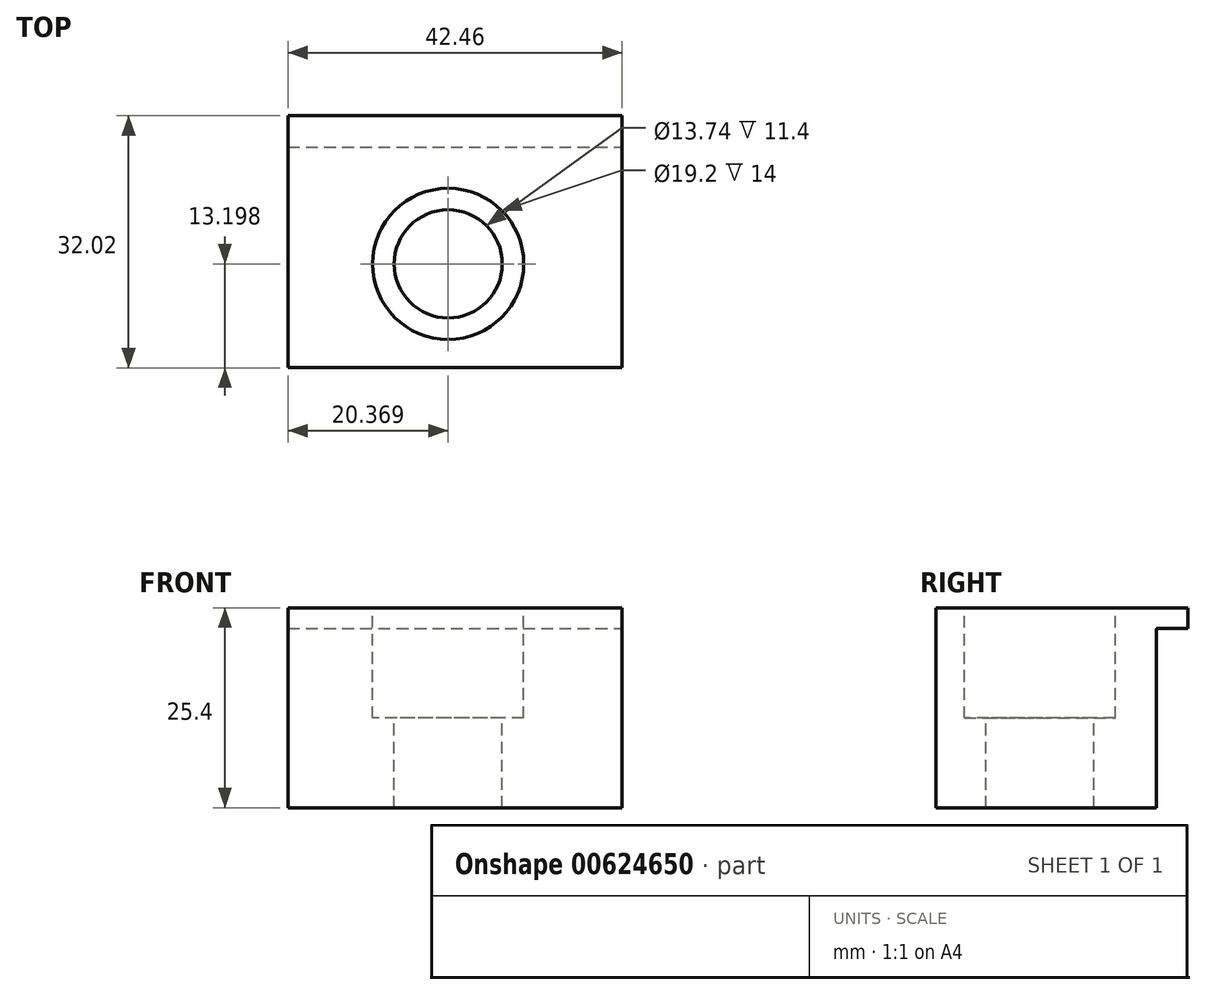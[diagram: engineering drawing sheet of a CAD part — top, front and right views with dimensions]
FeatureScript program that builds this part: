
annotation { "Feature Type Name" : "Feature", "Feature Type Description" : "" }
export const myFeature = defineFeature(function(context is Context, id is Id, definition is map)
    precondition{}
    {
        {
            var Q0;
            Q0=qCreatedBy(makeId("Top.planeOp"),FACE);
            var sketch = newSketch(context, id + "F0", { "sketchPlane" : qUnion([Q0])});
            skLineSegment(sketch, "E0.bottom", {"start": v(-47.59, 38.49) * mm, "end": v(-5.13, 38.49) * mm});
            skLineSegment(sketch, "E0.top", {"start": v(-47.59, 10.47) * mm, "end": v(-5.13, 10.47) * mm});
            skLineSegment(sketch, "E0.left", {"start": v(-47.59, 38.49) * mm, "end": v(-47.59, 10.47) * mm});
            skLineSegment(sketch, "E0.right", {"start": v(-5.13, 38.49) * mm, "end": v(-5.13, 10.47) * mm});
            skSolve(sketch);
        }
        {
            var Q0;
            Q0=makeQuery(id+"F0.imprint","IMPRINT",FACE,{"disambiguationData":[TD([[makeQuery(id+"F0.imprint","IMPRINT",EDGE,{"derivedFrom":sQuery(id+"F0.wireOp",EDGE,"E0.bottom")}),-1.0]])]});
            extrude(context, id + "F1", {"entities" : qUnion([Q0]), "depth" : 25.4 * mm, "offsetDistance" : 25 * mm});
        }
        {
            var Q0;
            Q0=makeQuery(id+"F1.opExtrude","CAP_FACE",FACE,{"disambiguationData":[OSD([sQuery(id+"F0.wireOp",EDGE,"E0.bottom"),sQuery(id+"F0.wireOp",EDGE,"E0.top"),sQuery(id+"F0.wireOp",EDGE,"E0.left"),sQuery(id+"F0.wireOp",EDGE,"E0.right")])],"isStart":false});
            var sketch = newSketch(context, id + "F2", { "sketchPlane" : qUnion([Q0])});
            skPoint(sketch, "E1", {"position": v(-27.22, 23.67) * mm});
            skSolve(sketch);
        }
        {
            var Q0;
            Q0=sQuery(id+"F2.wireOp",VERTEX,"E1");
            var Q1;
            Q1=makeQuery(id+"F1.opExtrude","SWEPT_BODY",BODY,{"disambiguationData":[OSD([sQuery(id+"F0.wireOp",EDGE,"E0.bottom"),sQuery(id+"F0.wireOp",EDGE,"E0.top"),sQuery(id+"F0.wireOp",EDGE,"E0.left"),sQuery(id+"F0.wireOp",EDGE,"E0.right")])]});
            hole(context, id + "F3", {"style" : HoleStyle.C_BORE, "endStyle" : HoleEndStyle.THROUGH, "holeDiameter" : 13.74 * mm, "cBoreDiameter" : 19.2 * mm, "cBoreDepth" : 14 * mm, "majorDiameter" : 5 * mm, "isTappedThrough" : true, "tappedDepth" : 12 * mm, "tapClearance" : 3, "startFromSketch" : true, "locations" : qUnion([Q0]), "scope" : qUnion([Q1])});
        }
        {
            var Q0;
            Q0=makeQuery(id+"F1.opExtrude","SWEPT_FACE",FACE,{"disambiguationData":[OSD([sQuery(id+"F0.wireOp",EDGE,"E0.bottom")])]});
            var sketch = newSketch(context, id + "F4", { "sketchPlane" : qUnion([Q0])});
            skLineSegment(sketch, "E2.bottom", {"start": v(47.59, 25.4) * mm, "end": v(5.13, 25.4) * mm});
            skLineSegment(sketch, "E2.top", {"start": v(47.59, 22.81) * mm, "end": v(5.13, 22.81) * mm});
            skLineSegment(sketch, "E2.left", {"start": v(47.59, 25.4) * mm, "end": v(47.59, 22.81) * mm});
            skLineSegment(sketch, "E2.right", {"start": v(5.13, 25.4) * mm, "end": v(5.13, 22.81) * mm});
            skSolve(sketch);
        }
        {
            var Q0;
            Q0=makeQuery(id+"F4.imprint","IMPRINT",FACE,{"disambiguationData":[TD([[makeQuery(id+"F4.imprint","IMPRINT",EDGE,{"derivedFrom":sQuery(id+"F4.wireOp",EDGE,"E2.bottom")}),1.0]])]});
            extrude(context, id + "F5", {"entities" : qUnion([Q0]), "operationType" : NewBodyOperationType.ADD, "depth" : 4 * mm, "offsetDistance" : 25 * mm});
        }
    });
